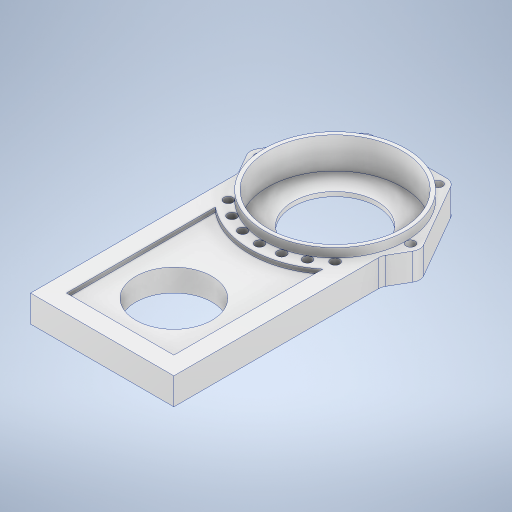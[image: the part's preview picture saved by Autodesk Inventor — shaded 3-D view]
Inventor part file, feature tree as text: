
AUTODESK INVENTOR PART (.ipt)
format: ipt  version: 2024 (Build 280153000, 153)  size: 424,960 bytes
history: native  units: mm
features: extrude x10, sketch x10, fillet x1, projected_geometry x1
ambient origin geometry x8: Origin, YZ Plane, XZ Plane, XY Plane, X Axis, Y Axis, Z Axis, Center Point
bodies: Solid1 (feature_tree)
feature tree (22):
  extrude  "Extrusion1"  Depth=160.0mm
  extrude  "Extrusion2"  Depth=30.0mm TaperAngle=0.0deg
  sketch  "Sketch3"  dims[d5=150.0mm d6=40.0mm d7=0.0mm]
  extrude  "Extrusion3"  Depth=40.0mm TaperAngle=0.0deg
  extrude  "Extrusion4"  Depth=10.0mm
  extrude  "Extrusion5"  Depth=5.0mm TaperAngle=0.0deg
  fillet  "Fillet1"  Radius=60.0mm
  extrude  "Extrusion6"  Depth=30.0mm TaperAngle=0.0deg
  extrude  "Extrusion7"  Depth=12.0mm
  extrude  "Extrusion8"  Depth=20.0mm
  extrude  "Extrusion9"  Depth=5.0mm
  extrude  "Extrusion10"  Depth=30.0mm
  sketch  "Sketch1"  dims[d0=250.0mm d1=160.0mm]
  sketch  "Sketch2"  dims[d2=160.0mm d3=30.0mm d4=0.0mm]
  sketch  "Sketch4"  dims[d8=10.0mm d9=94.0mm]
  sketch  "Sketch5"  dims[d10=150.0mm d11=5.0mm d12=0.0mm d13=60.0mm d15=360.0deg]
  sketch  "Sketch6"  dims[d18=60.0mm d19=360.0deg d20=30.0mm d21=0.0mm]
  projected_geometry  "Projected Loop1"
  sketch  "Sketch7"  dims[d22=30.0mm d23=0.0mm d24=12.0mm]
  sketch  "Sketch8"  dims[d25=20.0mm d26=190.0mm]
  sketch  "Sketch9"  dims[d27=5.0mm d28=0.0mm d29=150.0mm]
  sketch  "Sketch10"  dims[d30=10.0mm d31=0.0mm d32=84.286mm d33=240.0mm d35=360.0deg d37=35.0mm d38=0.0mm d39=10.0mm d40=85.0mm d41=40.0mm d42=0.0mm d43=30.0mm d44=0.0mm d17=0.5mm]
